# Revit family: Magnuson-Butler-CoatRack+
name_source: partatom
category: Furniture
units: mm (PartAtom-declared; Revit-internal decimal feet)

## family parameters
Always vertical = Yes
Cut with Voids When Loaded = No
OmniClass Number = 23.40.20.00
OmniClass Title = General Furniture and Specialties
Room Calculation Point = No
Shared = No
Work Plane-Based = No

## types (1)
- BUTLER
    Assembly Code = E2020200
    Base Finish = MAG - Steel Painted
    Default Elevation = 0"
    Depth = 18 7/8"
    Description = Painted steel coat rack with unique zig-zag base. 59 1/16” x 21 5/8” x 18 7/8”
    Frame Finish = MAG - Steel Painted
    Height = 59 1/16"
    Keynote = 12500
    Low Emitting Finish = Yes
    Low Emitting Material = Yes
    Manufacturer = Magnuson Group
    Model = BUTLER
    Percentage of Recycled Content = 0
    Product Documentation Link = https://magnusongroup.com
    Revit Model Built By = https://servex-us.com
    Salvage or Reuse = Yes
    Type Comments = Coat Rack
    URL = https://magnusongroup.com
    Width = 21 5/8"

## geometry (parser evidence)
native form markers: Sweep x6
no freeform markers — native parametric forms only
